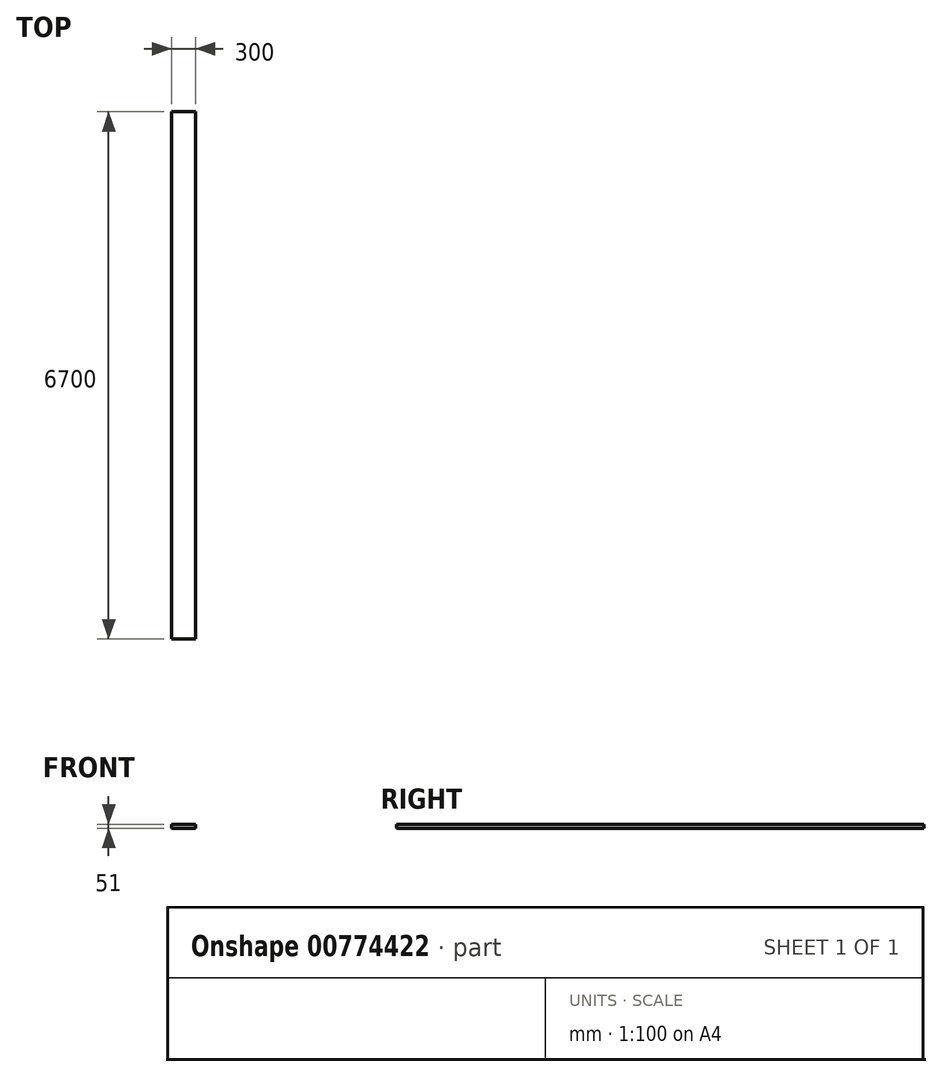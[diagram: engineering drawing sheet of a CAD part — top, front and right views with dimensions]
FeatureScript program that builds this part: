
annotation { "Feature Type Name" : "Feature", "Feature Type Description" : "" }
export const myFeature = defineFeature(function(context is Context, id is Id, definition is map)
    precondition{}
    {
        {
            var Q0;
            Q0=qCreatedBy(makeId("Front.planeOp"),FACE);
            var sketch = newSketch(context, id + "F0", { "sketchPlane" : qUnion([Q0])});
            skLineSegment(sketch, "E0.bottom", {"start": v(0, 0) * mm, "end": v(300, 0) * mm});
            skLineSegment(sketch, "E0.top", {"start": v(0, 51) * mm, "end": v(300, 51) * mm});
            skLineSegment(sketch, "E0.left", {"start": v(0, 0) * mm, "end": v(0, 51) * mm});
            skLineSegment(sketch, "E0.right", {"start": v(300, 0) * mm, "end": v(300, 51) * mm});
            skSolve(sketch);
        }
        {
            var Q0;
            Q0=qSketchRegion(id+"F0",true);
            extrude(context, id + "F1", {"entities" : qUnion([Q0]), "depth" : 6700 * mm, "offsetDistance" : 25 * mm});
        }
    });
